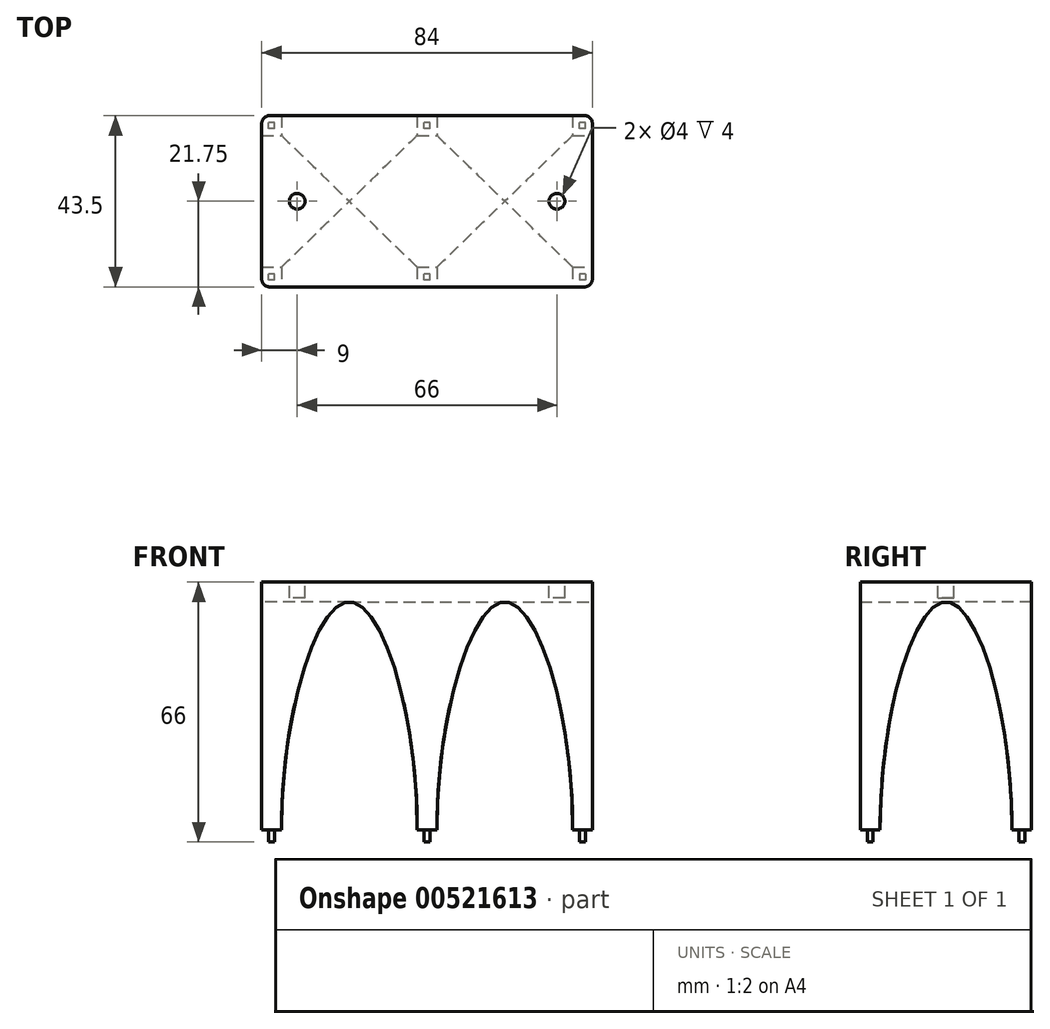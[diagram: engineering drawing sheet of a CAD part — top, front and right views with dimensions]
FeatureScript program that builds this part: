
annotation { "Feature Type Name" : "Feature", "Feature Type Description" : "" }
export const myFeature = defineFeature(function(context is Context, id is Id, definition is map)
    precondition{}
    {
        {
            var Q0;
            Q0=qCreatedBy(makeId("Right.planeOp"),FACE);
            var sketch = newSketch(context, id + "F0", { "sketchPlane" : qUnion([Q0])});
            skLineSegment(sketch, "E0.0", {"start": v(0, 3) * mm, "end": v(21, 3) * mm});
            skLineSegment(sketch, "E1.bottom", {"start": v(0, 63) * mm, "end": v(43.5, 63) * mm});
            skLineSegment(sketch, "E1.top", {"start": v(0, 66) * mm, "end": v(43.5, 66) * mm});
            skLineSegment(sketch, "E1.left", {"start": v(0, 63) * mm, "end": v(0, 66) * mm});
            skLineSegment(sketch, "E1.right", {"start": v(43.5, 63) * mm, "end": v(43.5, 66) * mm});
            skLineSegment(sketch, "E2", {"start": v(43.5, 63) * mm, "end": v(43.5, 3) * mm});
            skLineSegment(sketch, "E3", {"start": v(0, 63) * mm, "end": v(0, 3) * mm});
            skLineSegment(sketch, "E4", {"start": v(21, 3) * mm, "end": v(43.5, 3) * mm});
            skSolve(sketch);
        }
        {
            var Q0;
            Q0=makeQuery(id+"F0.imprint","IMPRINT",FACE,{"disambiguationData":[TD([[makeQuery(id+"F0.imprint","IMPRINT",EDGE,{"derivedFrom":sQuery(id+"F0.wireOp",EDGE,"E1.bottom")}),1.0]])]});
            var Q1;
            Q1=makeQuery(id+"F0.imprint","IMPRINT",FACE,{"disambiguationData":[TD([[makeQuery(id+"F0.imprint","IMPRINT",EDGE,{"derivedFrom":sQuery(id+"F0.wireOp",EDGE,"r5ec0JXA-QCaR-e4nW-opJY-GhlmDigo4CW7")}),1.0]])]});
            var Q2;
            Q2=makeQuery(id+"F0.imprint","IMPRINT",FACE,{"disambiguationData":[TD([[makeQuery(id+"F0.imprint","IMPRINT",EDGE,{"derivedFrom":sQuery(id+"F0.wireOp",EDGE,"E0.0")}),1.0]])]});
            var Q3;
            {var subQ3=sQuery(id+"F0.wireOp",EDGE,"2d6a4896-3aa3-4e97-b98b-c350a894f704.0");Q3=makeQuery(id+"F0.imprint","IMPRINT",FACE,{"disambiguationData":[TD([[makeQuery(id+"F0.imprint","IMPRINT",EDGE,{"derivedFrom":subQ3}),1.0]])]});}
            extrude(context, id + "F1", {"entities" : qUnion([Q0, Q1, Q2, Q3]), "oppositeDirection" : true, "depth" : 84 * mm, "offsetDistance" : 25 * mm});
        }
        {
            var Q0;
            Q0=qCreatedBy(makeId("Right.planeOp"),FACE);
            var sketch = newSketch(context, id + "F2", { "sketchPlane" : qUnion([Q0])});
            skPoint(sketch, "E5.0", {"position": v(0, 66) * mm});
            skPoint(sketch, "E6.0", {"position": v(43.5, 66) * mm});
            skPoint(sketch, "E7.0", {"position": v(43.5, 3) * mm});
            skPoint(sketch, "E8.0", {"position": v(0, 3) * mm});
            skLineSegment(sketch, "E9.bottom", {"start": v(0, 66) * mm, "end": v(43.5, 66) * mm, "construction": true});
            skLineSegment(sketch, "E9.top", {"start": v(0, 3) * mm, "end": v(5, 3) * mm, "construction": true});
            skLineSegment(sketch, "E9.left", {"start": v(0, 66) * mm, "end": v(0, 3) * mm, "construction": true});
            skLineSegment(sketch, "E9.right", {"start": v(43.5, 66) * mm, "end": v(43.5, 3) * mm, "construction": true});
            skLineSegment(sketch, "E10.0", {"start": v(5, 61) * mm, "end": v(5, 3) * mm, "construction": true});
            skLineSegment(sketch, "E10.1", {"start": v(5, 61) * mm, "end": v(38.5, 61) * mm, "construction": true});
            skLineSegment(sketch, "E10.2", {"start": v(38.5, 61) * mm, "end": v(38.5, 3) * mm, "construction": true});
            skFitSpline(sketch, "E11", {"points": [v(5, 3) * mm, v(21.75, 61) * mm, v(38.5, 3) * mm], "startDerivative": vector(0, 174) * mm, "endDerivative": vector(0, -174) * mm});
            skLineSegment(sketch, "E12.trimOffspring", {"start": v(38.5, 3) * mm, "end": v(43.5, 3) * mm, "construction": true});
            skLineSegment(sketch, "E13", {"start": v(5, 3) * mm, "end": v(38.5, 3) * mm});
            skSolve(sketch);
        }
        {
            var Q0;
            Q0 = qSketchRegion(id + "F2", true);
            var Q1;
            Q1=makeQuery(id+"F1.opExtrude","CAP_FACE",FACE,{"disambiguationData":[OSD([sQuery(id+"F0.wireOp",EDGE,"r5ec0JXA-QCaR-e4nW-opJY-GhlmDigo4CW7"),sQuery(id+"F0.wireOp",EDGE,"Mi6IbXjD-3L24-eetL-wy1F-uWNF9xTKTrjE"),sQuery(id+"F0.wireOp",EDGE,"5f37b275-18ff-4fa8-b2e3-1234a7435308.0"),sQuery(id+"F0.wireOp",EDGE,"a0fe2f97-68cd-4c7f-a408-543a71d82a41"),sQuery(id+"F0.wireOp",EDGE,"R4lYrwIj-TE4H-ftSf-smYm-KvcSFDlPldXV"),sQuery(id+"F0.wireOp",EDGE,"ABOKRz2A-O9Wl-NYz3-LtdV-byAFksUtFqJd"),sQuery(id+"F0.wireOp",EDGE,"E1.top"),sQuery(id+"F0.wireOp",EDGE,"E1.left"),sQuery(id+"F0.wireOp",EDGE,"E1.right"),sQuery(id+"F0.wireOp",EDGE,"E2"),sQuery(id+"F0.wireOp",EDGE,"E3"),sQuery(id+"F0.wireOp",EDGE,"E4"),sQuery(id+"F0.wireOp",EDGE,"2d6a4896-3aa3-4e97-b98b-c350a894f704.0")])],"isStart":false});
            extrude(context, id + "F3", {"entities" : qUnion([Q0]), "operationType" : NewBodyOperationType.REMOVE, "endBound" : BoundingType.UP_TO_SURFACE, "oppositeDirection" : true, "depth" : 25 * mm, "endBoundEntityFace" : qUnion([Q1]), "offsetDistance" : 25 * mm});
        }
        {
            var Q0;
            Q0=qCreatedBy(makeId("Front.planeOp"),FACE);
            var sketch = newSketch(context, id + "F4", { "sketchPlane" : qUnion([Q0])});
            skLineSegment(sketch, "E14.1", {"start": v(-79, 61) * mm, "end": v(-44.5, 61) * mm, "construction": true});
            skLineSegment(sketch, "E15.trimOffspring", {"start": v(-39.5, 61) * mm, "end": v(-5, 61) * mm, "construction": true});
            skLineSegment(sketch, "E16.0", {"start": v(-79, 3) * mm, "end": v(-44.5, 3) * mm});
            skPoint(sketch, "E17.orphan", {"position": v(-84, 3) * mm});
            skPoint(sketch, "E18.orphan", {"position": v(0, 3) * mm});
            skLineSegment(sketch, "E19", {"start": v(-79, 61) * mm, "end": v(-79, 3) * mm, "construction": true});
            skLineSegment(sketch, "E20", {"start": v(-5, 61) * mm, "end": v(-5, 3) * mm, "construction": true});
            skLineSegment(sketch, "E21", {"start": v(-44.5, 61) * mm, "end": v(-44.5, 3) * mm, "construction": true});
            skLineSegment(sketch, "E22", {"start": v(-39.5, 61) * mm, "end": v(-39.5, 3) * mm, "construction": true});
            skLineSegment(sketch, "E23.trimOffspring", {"start": v(-39.5, 3) * mm, "end": v(-5, 3) * mm});
            skFitSpline(sketch, "E24", {"points": [v(-79, 3) * mm, v(-61.75, 61) * mm, v(-44.5, 3) * mm], "startDerivative": vector(0, 174) * mm, "endDerivative": vector(0, -174) * mm});
            skFitSpline(sketch, "E25", {"points": [v(-39.5, 3) * mm, v(-22.25, 61) * mm, v(-5, 3) * mm], "startDerivative": vector(0, 174) * mm, "endDerivative": vector(0, -174) * mm});
            skSolve(sketch);
        }
        {
            var Q0;
            Q0=makeQuery(id+"F4.imprint","IMPRINT",FACE,{"disambiguationData":[TD([[makeQuery(id+"F4.imprint","IMPRINT",EDGE,{"derivedFrom":sQuery(id+"F4.wireOp",EDGE,"E16.0")}),1.0]])]});
            var Q1;
            Q1=makeQuery(id+"F4.imprint","IMPRINT",FACE,{"disambiguationData":[TD([[makeQuery(id+"F4.imprint","IMPRINT",EDGE,{"derivedFrom":sQuery(id+"F4.wireOp",EDGE,"E23.trimOffspring")}),1.0]])]});
            var Q2;
            Q2=makeQuery(id+"F1.opExtrude","SWEPT_FACE",FACE,{"disambiguationData":[OSD([sQuery(id+"F0.wireOp",EDGE,"E1.right"),sQuery(id+"F0.wireOp",EDGE,"E2")])]});
            extrude(context, id + "F5", {"entities" : qUnion([Q0, Q1]), "operationType" : NewBodyOperationType.REMOVE, "endBound" : BoundingType.UP_TO_SURFACE, "oppositeDirection" : true, "depth" : 25 * mm, "endBoundEntityFace" : qUnion([Q2]), "offsetDistance" : 25 * mm});
        }
        {
            var Q0;
            Q0=makeQuery(id+"F1.opExtrude","CAP_EDGE",EDGE,{"disambiguationData":[OSD([sQuery(id+"F0.wireOp",EDGE,"R4lYrwIj-TE4H-ftSf-smYm-KvcSFDlPldXV"),sQuery(id+"F0.wireOp",EDGE,"E1.left"),sQuery(id+"F0.wireOp",EDGE,"E3")])],"isStart":true});
            var Q1;
            Q1=makeQuery(id+"F1.opExtrude","CAP_EDGE",EDGE,{"disambiguationData":[OSD([sQuery(id+"F0.wireOp",EDGE,"R4lYrwIj-TE4H-ftSf-smYm-KvcSFDlPldXV"),sQuery(id+"F0.wireOp",EDGE,"E1.left"),sQuery(id+"F0.wireOp",EDGE,"E3")])],"isStart":false});
            var Q2;
            Q2=makeQuery(id+"F1.opExtrude","CAP_EDGE",EDGE,{"disambiguationData":[OSD([sQuery(id+"F0.wireOp",EDGE,"E1.right"),sQuery(id+"F0.wireOp",EDGE,"E2")])],"isStart":true});
            var Q3;
            Q3=makeQuery(id+"F1.opExtrude","CAP_EDGE",EDGE,{"disambiguationData":[OSD([sQuery(id+"F0.wireOp",EDGE,"E1.right"),sQuery(id+"F0.wireOp",EDGE,"E2")])],"isStart":false});
            fillet(context, id + "F6", {"entities" : qUnion([Q0, Q1, Q2, Q3]), "radius" : 2 * mm, "tangentPropagation" : true, "allowEdgeOverflow" : false});
        }
        {
            var Q0;
            Q0=makeQuery(id+"F1.opExtrude","SWEPT_FACE",FACE,{"disambiguationData":[OSD([sQuery(id+"F0.wireOp",EDGE,"E1.top")])]});
            var sketch = newSketch(context, id + "F7", { "sketchPlane" : qUnion([Q0])});
            skLineSegment(sketch, "E26.0.0", {"start": v(-82, 0) * mm, "end": v(-2, 0) * mm, "construction": true});
            skArc(sketch, "E26.0.1", {"start": v(-2, 0) * mm, "mid": v(-0.59, 0.59) * mm, "end": v(0, 2) * mm, "construction": true});
            skLineSegment(sketch, "E26.0.2", {"start": v(0, 2) * mm, "end": v(0, 41.5) * mm, "construction": true});
            skArc(sketch, "E26.0.3", {"start": v(0, 41.5) * mm, "mid": v(-0.59, 42.91) * mm, "end": v(-2, 43.5) * mm, "construction": true});
            skLineSegment(sketch, "E26.0.4", {"start": v(-2, 43.5) * mm, "end": v(-82, 43.5) * mm, "construction": true});
            skArc(sketch, "E26.0.5", {"start": v(-82, 43.5) * mm, "mid": v(-83.41, 42.91) * mm, "end": v(-84, 41.5) * mm, "construction": true});
            skLineSegment(sketch, "E26.0.6", {"start": v(-84, 41.5) * mm, "end": v(-84, 2) * mm, "construction": true});
            skArc(sketch, "E26.0.7", {"start": v(-84, 2) * mm, "mid": v(-83.41, 0.59) * mm, "end": v(-82, 0) * mm, "construction": true});
            skLineSegment(sketch, "E27", {"start": v(0, 21.75) * mm, "end": v(-9, 21.75) * mm, "construction": true});
            skLineSegment(sketch, "E28", {"start": v(-84, 21.75) * mm, "end": v(-75, 21.75) * mm, "construction": true});
            skCircle(sketch, "E29", {"center": v(-75, 21.75) * mm, "radius": 2 * mm});
            skCircle(sketch, "E30", {"center": v(-9, 21.75) * mm, "radius": 2 * mm});
            skSolve(sketch);
        }
        {
            var Q0;
            Q0 = qSketchRegion(id + "F7", true);
            extrude(context, id + "F8", {"entities" : qUnion([Q0]), "operationType" : NewBodyOperationType.REMOVE, "oppositeDirection" : true, "depth" : 4 * mm, "offsetDistance" : 25 * mm});
        }
        {
            var Q0;
            {var subQ0=sQuery(id+"F0.wireOp",EDGE,"E3");var subQ1=sQuery(id+"F0.wireOp",EDGE,"E1.left");var subQ2=makeQuery(id+"F1.opExtrude","SWEPT_FACE",FACE,{"disambiguationData":[OSD([subQ1,subQ0])]});var subQ3=makeQuery(id+"F3.opExtrude","SWEPT_FACE",FACE,{"disambiguationData":[OSD([sQuery(id+"F2.wireOp",EDGE,"E11")])]});var subQ4=sQuery(id+"F0.wireOp",EDGE,"E4");var subQ8=sQuery(id+"F0.wireOp",EDGE,"E0.0");Q0=makeQuery(id+"F5.boolean.opBoolean","SPLIT",FACE,{"disambiguationData":[TD([subQ2,makeQuery(id+"F3.boolean.opBoolean","COPY",FACE,{"derivedFrom":subQ3}),makeQuery(id+"F5.opExtrude","SWEPT_FACE",FACE,{"disambiguationData":[OSD([sQuery(id+"F4.wireOp",EDGE,"E24")])]}),makeQuery(id+"F5.opExtrude","SWEPT_FACE",FACE,{"disambiguationData":[OSD([sQuery(id+"F4.wireOp",EDGE,"E25")])]})])],"derivedFrom":makeQuery(id+"F3.boolean.opBoolean","SPLIT",FACE,{"disambiguationData":[TD([subQ2])],"derivedFrom":makeQuery(id+"F1.opExtrude","SWEPT_FACE",FACE,{"disambiguationData":[OSD([subQ8,subQ4])]})})});}
            var sketch = newSketch(context, id + "F9", { "sketchPlane" : qUnion([Q0])});
            skLineSegment(sketch, "E31.0.0", {"start": v(-44.5, 0) * mm, "end": v(-44.5, -5) * mm, "construction": true});
            skLineSegment(sketch, "E31.0.1", {"start": v(-44.5, -5) * mm, "end": v(-39.5, -5) * mm, "construction": true});
            skLineSegment(sketch, "E31.0.2", {"start": v(-39.5, -5) * mm, "end": v(-39.5, 0) * mm, "construction": true});
            skLineSegment(sketch, "E31.0.3", {"start": v(-39.5, 0) * mm, "end": v(-44.5, 0) * mm, "construction": true});
            skLineSegment(sketch, "E32.0.0", {"start": v(0, -5) * mm, "end": v(0, -2) * mm, "construction": true});
            skArc(sketch, "E32.0.1", {"start": v(0, -2) * mm, "mid": v(-0.59, -0.59) * mm, "end": v(-2, 0) * mm, "construction": true});
            skLineSegment(sketch, "E32.0.2", {"start": v(-2, 0) * mm, "end": v(-5, 0) * mm, "construction": true});
            skLineSegment(sketch, "E32.0.3", {"start": v(-5, 0) * mm, "end": v(-5, -5) * mm, "construction": true});
            skLineSegment(sketch, "E32.0.4", {"start": v(-5, -5) * mm, "end": v(0, -5) * mm, "construction": true});
            skLineSegment(sketch, "E33.0.0", {"start": v(-5, -43.5) * mm, "end": v(-2, -43.5) * mm, "construction": true});
            skArc(sketch, "E33.0.1", {"start": v(-2, -43.5) * mm, "mid": v(-0.59, -42.91) * mm, "end": v(0, -41.5) * mm, "construction": true});
            skLineSegment(sketch, "E33.0.2", {"start": v(0, -41.5) * mm, "end": v(0, -38.5) * mm, "construction": true});
            skLineSegment(sketch, "E33.0.3", {"start": v(0, -38.5) * mm, "end": v(-5, -38.5) * mm, "construction": true});
            skLineSegment(sketch, "E33.0.4", {"start": v(-5, -38.5) * mm, "end": v(-5, -43.5) * mm, "construction": true});
            skLineSegment(sketch, "E34.0.0", {"start": v(-44.5, -38.5) * mm, "end": v(-44.5, -43.5) * mm, "construction": true});
            skLineSegment(sketch, "E34.0.1", {"start": v(-44.5, -43.5) * mm, "end": v(-39.5, -43.5) * mm, "construction": true});
            skLineSegment(sketch, "E34.0.2", {"start": v(-39.5, -43.5) * mm, "end": v(-39.5, -38.5) * mm, "construction": true});
            skLineSegment(sketch, "E34.0.3", {"start": v(-39.5, -38.5) * mm, "end": v(-44.5, -38.5) * mm, "construction": true});
            skLineSegment(sketch, "E35.0.0", {"start": v(-84, -38.5) * mm, "end": v(-84, -41.5) * mm, "construction": true});
            skArc(sketch, "E35.0.1", {"start": v(-84, -41.5) * mm, "mid": v(-83.41, -42.91) * mm, "end": v(-82, -43.5) * mm, "construction": true});
            skLineSegment(sketch, "E35.0.2", {"start": v(-82, -43.5) * mm, "end": v(-79, -43.5) * mm, "construction": true});
            skLineSegment(sketch, "E35.0.3", {"start": v(-79, -43.5) * mm, "end": v(-79, -38.5) * mm, "construction": true});
            skLineSegment(sketch, "E35.0.4", {"start": v(-79, -38.5) * mm, "end": v(-84, -38.5) * mm, "construction": true});
            skLineSegment(sketch, "E36.0.0", {"start": v(-79, 0) * mm, "end": v(-82, 0) * mm, "construction": true});
            skArc(sketch, "E36.0.1", {"start": v(-82, 0) * mm, "mid": v(-83.41, -0.59) * mm, "end": v(-84, -2) * mm, "construction": true});
            skLineSegment(sketch, "E36.0.2", {"start": v(-84, -2) * mm, "end": v(-84, -5) * mm, "construction": true});
            skLineSegment(sketch, "E36.0.3", {"start": v(-84, -5) * mm, "end": v(-79, -5) * mm, "construction": true});
            skLineSegment(sketch, "E36.0.4", {"start": v(-79, -5) * mm, "end": v(-79, 0) * mm, "construction": true});
            skLineSegment(sketch, "E37.bottom", {"start": v(-41.25, -1.75) * mm, "end": v(-42.75, -1.75) * mm});
            skLineSegment(sketch, "E37.top", {"start": v(-41.25, -3.25) * mm, "end": v(-42.75, -3.25) * mm});
            skLineSegment(sketch, "E37.left", {"start": v(-41.25, -1.75) * mm, "end": v(-41.25, -3.25) * mm});
            skLineSegment(sketch, "E37.right", {"start": v(-42.75, -1.75) * mm, "end": v(-42.75, -3.25) * mm});
            skPoint(sketch, "E37.middle", {"position": v(-42, -2.5) * mm});
            skPoint(sketch, "E37.middle.positionSnap0", {"position": v(-42, 0) * mm});
            skPoint(sketch, "E37.middle.positionSnap1", {"position": v(-44.5, -2.5) * mm});
            skPoint(sketch, "E37.centerSnap0", {"position": v(-42, 0) * mm});
            skPoint(sketch, "E37.centerSnap1", {"position": v(-44.5, -2.5) * mm});
            skLineSegment(sketch, "E38.bottom", {"start": v(-1.75, -3.25) * mm, "end": v(-3.25, -3.25) * mm});
            skLineSegment(sketch, "E38.top", {"start": v(-1.75, -1.75) * mm, "end": v(-3.25, -1.75) * mm});
            skLineSegment(sketch, "E38.left", {"start": v(-1.75, -3.25) * mm, "end": v(-1.75, -1.75) * mm});
            skLineSegment(sketch, "E38.right", {"start": v(-3.25, -3.25) * mm, "end": v(-3.25, -1.75) * mm});
            skPoint(sketch, "E38.middle", {"position": v(-2.5, -2.5) * mm});
            skPoint(sketch, "E38.middle.positionSnap0", {"position": v(-2.5, -5) * mm});
            skPoint(sketch, "E38.middle.positionSnap1", {"position": v(-5, -2.5) * mm});
            skPoint(sketch, "E38.centerSnap0", {"position": v(-2.5, -5) * mm});
            skPoint(sketch, "E38.centerSnap1", {"position": v(-5, -2.5) * mm});
            skLineSegment(sketch, "E39.bottom", {"start": v(-1.75, -40.25) * mm, "end": v(-3.25, -40.25) * mm});
            skLineSegment(sketch, "E39.top", {"start": v(-1.75, -41.75) * mm, "end": v(-3.25, -41.75) * mm});
            skLineSegment(sketch, "E39.left", {"start": v(-1.75, -40.25) * mm, "end": v(-1.75, -41.75) * mm});
            skLineSegment(sketch, "E39.right", {"start": v(-3.25, -40.25) * mm, "end": v(-3.25, -41.75) * mm});
            skPoint(sketch, "E39.middle", {"position": v(-2.5, -41) * mm});
            skPoint(sketch, "E39.middle.positionSnap0", {"position": v(-2.5, -38.5) * mm});
            skPoint(sketch, "E39.middle.positionSnap1", {"position": v(-5, -41) * mm});
            skPoint(sketch, "E39.centerSnap0", {"position": v(-2.5, -38.5) * mm});
            skPoint(sketch, "E39.centerSnap1", {"position": v(-5, -41) * mm});
            skLineSegment(sketch, "E40.bottom", {"start": v(-41.25, -40.25) * mm, "end": v(-42.75, -40.25) * mm});
            skLineSegment(sketch, "E40.top", {"start": v(-41.25, -41.75) * mm, "end": v(-42.75, -41.75) * mm});
            skLineSegment(sketch, "E40.left", {"start": v(-41.25, -40.25) * mm, "end": v(-41.25, -41.75) * mm});
            skLineSegment(sketch, "E40.right", {"start": v(-42.75, -40.25) * mm, "end": v(-42.75, -41.75) * mm});
            skPoint(sketch, "E40.middle", {"position": v(-42, -41) * mm});
            skPoint(sketch, "E40.middle.positionSnap0", {"position": v(-44.5, -41) * mm});
            skPoint(sketch, "E40.middle.positionSnap1", {"position": v(-42, -38.5) * mm});
            skPoint(sketch, "E40.centerSnap0", {"position": v(-44.5, -41) * mm});
            skPoint(sketch, "E40.centerSnap1", {"position": v(-42, -38.5) * mm});
            skLineSegment(sketch, "E41.bottom", {"start": v(-80.75, -40.25) * mm, "end": v(-82.25, -40.25) * mm});
            skLineSegment(sketch, "E41.top", {"start": v(-80.75, -41.75) * mm, "end": v(-82.25, -41.75) * mm});
            skLineSegment(sketch, "E41.left", {"start": v(-80.75, -40.25) * mm, "end": v(-80.75, -41.75) * mm});
            skLineSegment(sketch, "E41.right", {"start": v(-82.25, -40.25) * mm, "end": v(-82.25, -41.75) * mm});
            skPoint(sketch, "E41.middle", {"position": v(-81.5, -41) * mm});
            skPoint(sketch, "E41.middle.positionSnap0", {"position": v(-79, -41) * mm});
            skPoint(sketch, "E41.middle.positionSnap1", {"position": v(-81.5, -38.5) * mm});
            skPoint(sketch, "E41.centerSnap0", {"position": v(-79, -41) * mm});
            skPoint(sketch, "E41.centerSnap1", {"position": v(-81.5, -38.5) * mm});
            skLineSegment(sketch, "E42.bottom", {"start": v(-80.75, -1.75) * mm, "end": v(-82.25, -1.75) * mm});
            skLineSegment(sketch, "E42.top", {"start": v(-80.75, -3.25) * mm, "end": v(-82.25, -3.25) * mm});
            skLineSegment(sketch, "E42.left", {"start": v(-80.75, -1.75) * mm, "end": v(-80.75, -3.25) * mm});
            skLineSegment(sketch, "E42.right", {"start": v(-82.25, -1.75) * mm, "end": v(-82.25, -3.25) * mm});
            skPoint(sketch, "E42.middle", {"position": v(-81.5, -2.5) * mm});
            skPoint(sketch, "E42.middle.positionSnap0", {"position": v(-79, -2.5) * mm});
            skPoint(sketch, "E42.middle.positionSnap1", {"position": v(-81.5, -5) * mm});
            skPoint(sketch, "E42.centerSnap0", {"position": v(-79, -2.5) * mm});
            skPoint(sketch, "E42.centerSnap1", {"position": v(-81.5, -5) * mm});
            skSolve(sketch);
        }
        {
            var Q0;
            Q0 = qSketchRegion(id + "F9", true);
            extrude(context, id + "F10", {"entities" : qUnion([Q0]), "operationType" : NewBodyOperationType.ADD, "depth" : 3 * mm, "offsetDistance" : 25 * mm});
        }
    });
